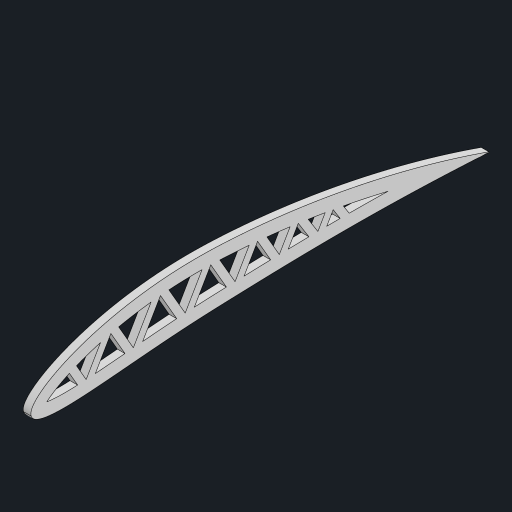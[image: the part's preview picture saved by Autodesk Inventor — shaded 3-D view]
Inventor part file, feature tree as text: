
AUTODESK INVENTOR PART (.ipt)
format: ipt  version: 2023 (Build 270158000, 158)  size: 254,464 bytes
history: native  units: mm
features: extrude x2, sketch x2, other x1
ambient origin geometry x8: Origin, YZ Plane, XZ Plane, XY Plane, X Axis, Y Axis, Z Axis, Center Point
bodies: Body1 (feature_tree)
feature tree (5):
  other  "ソリッド1"
  extrude  "押し出し1"  Depth=180.0mm
  extrude  "押し出し2"  Depth=3.0mm TaperAngle=0.0deg
  sketch  "スケッチ1"
  sketch  "スケッチ2"
